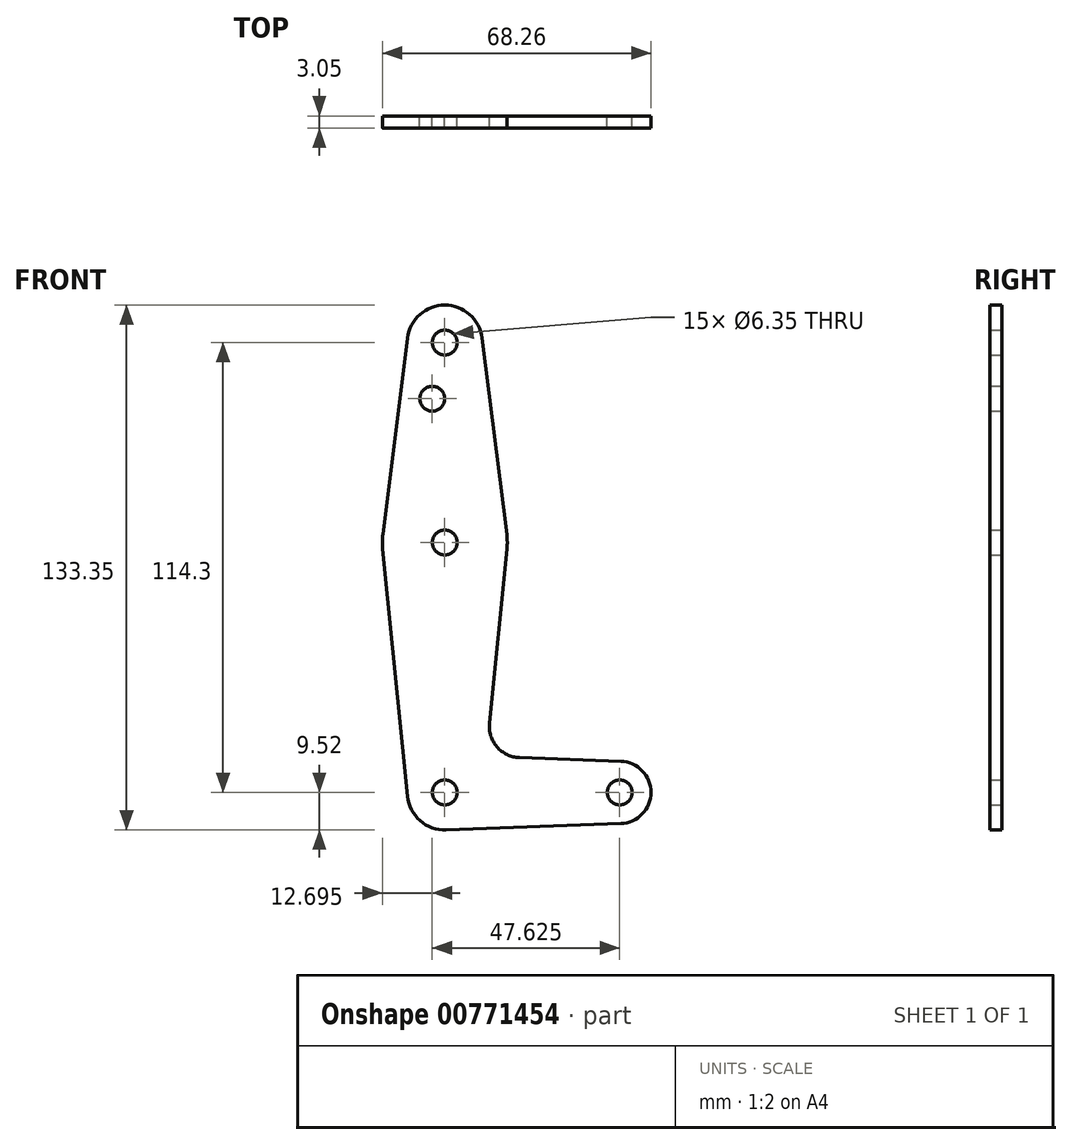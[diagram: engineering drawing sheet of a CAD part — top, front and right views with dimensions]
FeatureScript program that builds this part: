
annotation { "Feature Type Name" : "Feature", "Feature Type Description" : "" }
export const myFeature = defineFeature(function(context is Context, id is Id, definition is map)
    precondition{}
    {
        {
            var Q0;
            Q0=qCreatedBy(makeId("Front.planeOp"),FACE);
            var sketch = newSketch(context, id + "F0", { "sketchPlane" : qUnion([Q0])});
            skLineSegment(sketch, "E0", {"start": v(0, 0) * mm, "end": v(0, 114.3) * mm, "construction": true});
            skLineSegment(sketch, "E1", {"start": v(0, 0) * mm, "end": v(44.45, 0) * mm, "construction": true});
            skCircle(sketch, "E2", {"center": v(0, 114.3) * mm, "radius": 9.53 * mm});
            skCircle(sketch, "E3", {"center": v(0, 63.5) * mm, "radius": 15.88 * mm});
            skCircle(sketch, "E4", {"center": v(0, 0) * mm, "radius": 9.53 * mm});
            skCircle(sketch, "E5", {"center": v(44.45, 0) * mm, "radius": 7.94 * mm});
            skLineSegment(sketch, "E6", {"start": v(-9.48, -0.95) * mm, "end": v(-15.8, 61.91) * mm});
            skLineSegment(sketch, "E7", {"start": v(-15.75, 65.48) * mm, "end": v(-9.45, 115.5) * mm});
            skLineSegment(sketch, "E8", {"start": v(15.75, 65.48) * mm, "end": v(9.45, 115.5) * mm});
            skLineSegment(sketch, "E9", {"start": v(11.34, 17.6) * mm, "end": v(15.8, 61.91) * mm});
            skLineSegment(sketch, "E10", {"start": v(0.34, -9.52) * mm, "end": v(44.73, -7.93) * mm});
            skLineSegment(sketch, "E11", {"start": v(18.97, 8.85) * mm, "end": v(44.73, 7.93) * mm});
            skCircle(sketch, "E12", {"center": v(0, 114.3) * mm, "radius": 3.18 * mm});
            skCircle(sketch, "E13", {"center": v(0, 63.5) * mm, "radius": 3.18 * mm});
            skCircle(sketch, "E14", {"center": v(0, 0) * mm, "radius": 3.18 * mm});
            skCircle(sketch, "E15", {"center": v(44.45, 0) * mm, "radius": 3.18 * mm});
            skCircle(sketch, "E16", {"center": v(-3.18, 100.03) * mm, "radius": 3.18 * mm});
            skArc(sketch, "E17.filletArc", {"start": v(11.34, 17.6) * mm, "mid": v(13.26, 11.57) * mm, "end": v(18.97, 8.85) * mm});
            skSolve(sketch);
        }
        {
            var Q0;
            Q0 = qSketchRegion(id + "F0", true);
            extrude(context, id + "F1", {"entities" : qUnion([Q0]), "depth" : 3.05 * mm, "offsetDistance" : 25.4 * mm});
        }
    });
